# Revit family: RV 6120 00  Flopro Z2 Circular
name_source: partatom
category: Luminarias
revit_build: Autodesk Revit 2015 (Build: 20140606_1530(x64)
units: mm (PartAtom-declared; Revit-internal decimal feet)

## types (3) — shared parameters
Cambio de temperatura de color de luz atenuada = <Ninguno>
Diámetro de círculo de emisión = 97 mm
Fabricante = SECOM ILUMINACIÓN
Filtro de color = 16777215
Forma visible en renderización = No
Lámpara = LED Osram Duris
Ángulo de inclinación = 90.00°

## per-type parameters (varying)
| type | Archivo de red fotométrica | Comentarios de vataje | Descripción | Modelo | Óptica angulo de apertura |
| Flopro Z2 Circular  6W / 48º | 6120 00 06 84 FLOPRO Z2 LED CIRCULAR L48º 6W.IES | 6W | 6120 00 06 84 | Flopro Z2 Circular 6W | 48.00° |
| Flopro Z2 Circular 6W / 11º | 6120 00 06 84 11 FLOPRO Z2 LED CIRCULAR L11º 6W.IES | 6W | 6120 00 06 84 | Flopro Z2 Circular 6W | 11.00° |
| Flopro Z2 Circular orientable asimétrico 7W | 6110 00 07 84 FLOPRO Z2 LED CIRCULAR ASIMETRICO L48º 7W.IES | 7W | 6110 00 07 84 | Flopro Z2 Circular asimétrico 7W | 48.00° |
